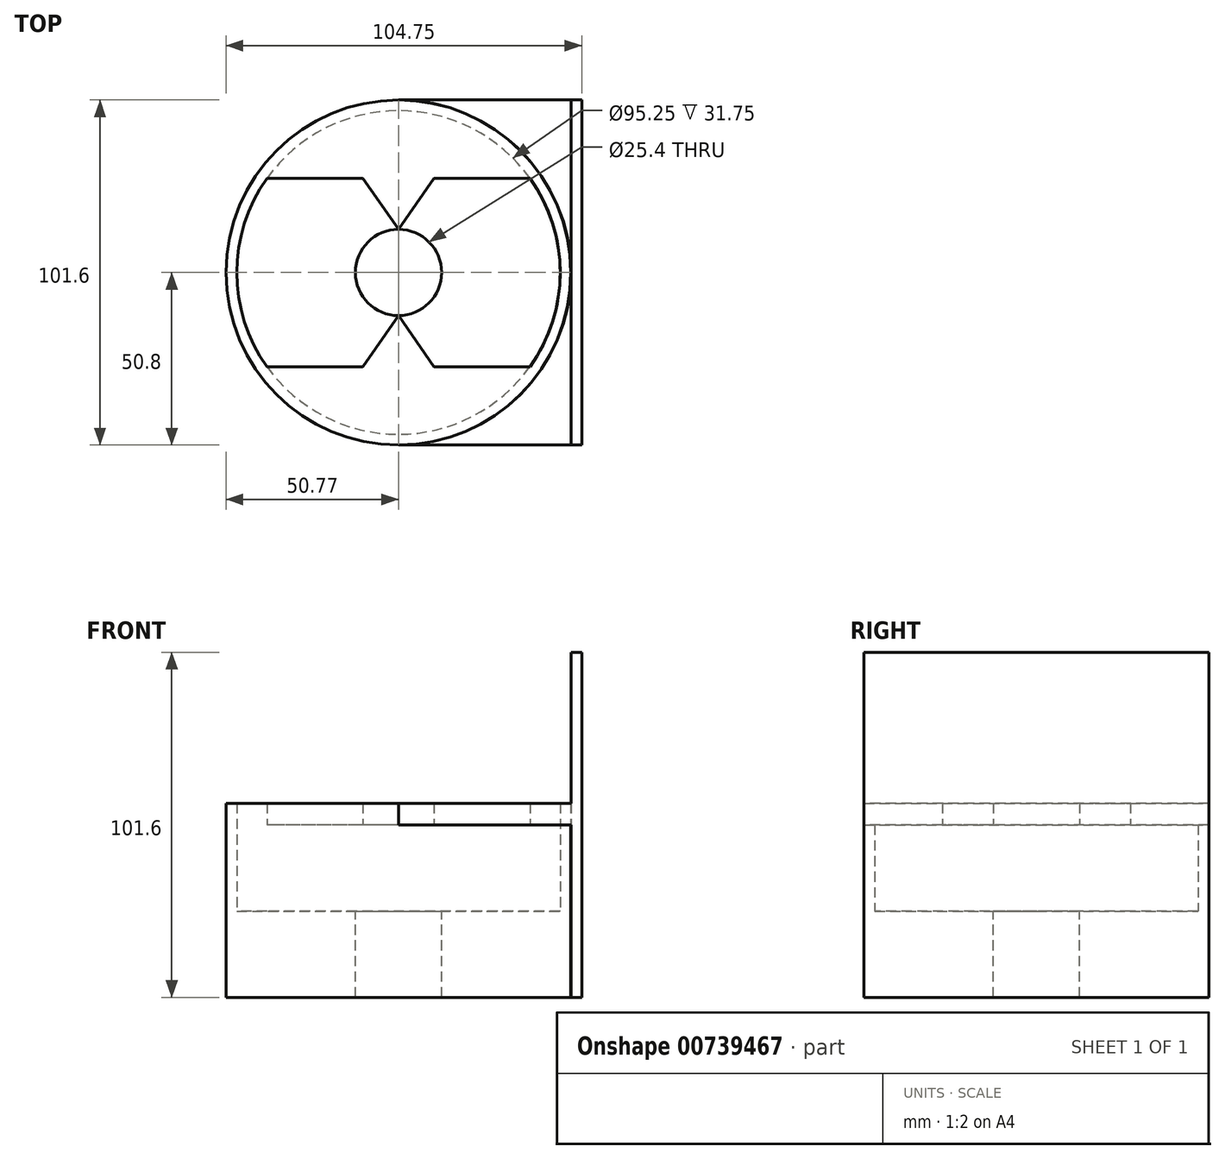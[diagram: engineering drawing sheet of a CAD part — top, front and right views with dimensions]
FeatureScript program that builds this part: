
annotation { "Feature Type Name" : "Feature", "Feature Type Description" : "" }
export const myFeature = defineFeature(function(context is Context, id is Id, definition is map)
    precondition{}
    {
        {
            var Q0;
            Q0=qCreatedBy(makeId("Top.planeOp"),FACE);
            var sketch = newSketch(context, id + "F0", { "sketchPlane" : qUnion([Q0])});
            skCircle(sketch, "E0", {"center": v(0, 0) * mm, "radius": 47.63 * mm});
            skCircle(sketch, "E1", {"center": v(0, 0) * mm, "radius": 50.8 * mm});
            skLineSegment(sketch, "E2.bottom", {"start": v(50.8, 50.8) * mm, "end": v(53.98, 50.8) * mm});
            skLineSegment(sketch, "E2.top", {"start": v(50.8, -50.8) * mm, "end": v(53.98, -50.8) * mm});
            skLineSegment(sketch, "E2.left", {"start": v(50.8, 50.8) * mm, "end": v(50.8, -50.8) * mm});
            skLineSegment(sketch, "E2.right", {"start": v(53.98, 50.8) * mm, "end": v(53.98, -50.8) * mm});
            skLineSegment(sketch, "E3", {"start": v(0, 50.8) * mm, "end": v(96.5, 50.8) * mm});
            skLineSegment(sketch, "E4", {"start": v(0, -50.8) * mm, "end": v(100.01, -50.8) * mm});
            skLineSegment(sketch, "E5", {"start": v(0, 50.8) * mm, "end": v(0, -50.8) * mm});
            skLineSegment(sketch, "E6", {"start": v(21.03, 42.73) * mm, "end": v(0, 12.7) * mm});
            skLineSegment(sketch, "E7", {"start": v(0, 12.7) * mm, "end": v(-21.03, 42.73) * mm});
            skLineSegment(sketch, "E8", {"start": v(21.03, -42.73) * mm, "end": v(0, -12.7) * mm});
            skLineSegment(sketch, "E9", {"start": v(0, -12.7) * mm, "end": v(-21.03, -42.73) * mm});
            skLineSegment(sketch, "E10", {"start": v(10.51, 27.72) * mm, "end": v(38.73, 27.72) * mm});
            skLineSegment(sketch, "E11", {"start": v(10.51, -27.72) * mm, "end": v(38.73, -27.72) * mm});
            skLineSegment(sketch, "E12", {"start": v(-10.51, 27.72) * mm, "end": v(-38.73, 27.72) * mm});
            skLineSegment(sketch, "E13", {"start": v(-10.51, -27.72) * mm, "end": v(-38.73, -27.72) * mm});
            skCircle(sketch, "E14", {"center": v(0, 0) * mm, "radius": 50.77 * mm});
            skSolve(sketch);
        }
        {
            var Q0;
            {var subQ3=sQuery(id+"F0.wireOp",EDGE,"E2.right");Q0=makeQuery(id+"F0.imprint","IMPRINT",FACE,{"disambiguationData":[TD([[makeQuery(id+"F0.imprint","IMPRINT",EDGE,{"derivedFrom":subQ3}),-1.0]])]});}
            extrude(context, id + "F1", {"entities" : qUnion([Q0]), "endBound" : BoundingType.SYMMETRIC, "depth" : 101.6 * mm, "offsetDistance" : 25.4 * mm});
        }
        {
            var Q0;
            {var subQ0=sQuery(id+"F0.wireOp",EDGE,"E3");var subQ3=sQuery(id+"F0.wireOp",EDGE,"E2.left");var subQ5=makeQuery(id+"F0.imprint","INTERSECT",VERTEX,{"derivedFrom":[subQ3,subQ0]});Q0=makeQuery(id+"F0.imprint","IMPRINT",FACE,{"disambiguationData":[TD([[makeQuery(id+"F0.imprint","IMPRINT",EDGE,{"disambiguationData":[TD([[subQ5,-1.0]])],"derivedFrom":subQ3}),-1.0]])]});}
            var Q1;
            {var subQ0=sQuery(id+"F0.wireOp",EDGE,"E4");var subQ3=sQuery(id+"F0.wireOp",EDGE,"E2.left");var subQ5=makeQuery(id+"F0.imprint","INTERSECT",VERTEX,{"derivedFrom":[subQ3,subQ0]});Q1=makeQuery(id+"F0.imprint","IMPRINT",FACE,{"disambiguationData":[TD([[makeQuery(id+"F0.imprint","IMPRINT",EDGE,{"disambiguationData":[TD([[subQ5,1.0]])],"derivedFrom":subQ3}),-1.0]])]});}
            var Q2;
            {var subQ0=sQuery(id+"F0.wireOp",EDGE,"E0");var subQ5=makeQuery(id+"F0.imprint","INTERSECT",VERTEX,{"derivedFrom":[subQ0,sQuery(id+"F0.wireOp",EDGE,"E6")]});Q2=makeQuery(id+"F0.imprint","IMPRINT",FACE,{"disambiguationData":[TD([[makeQuery(id+"F0.imprint","IMPRINT",EDGE,{"disambiguationData":[TD([[subQ5,1.0]])],"derivedFrom":subQ0}),-1.0]])]});}
            var Q3;
            {var subQ0=sQuery(id+"F0.wireOp",EDGE,"E0");var subQ4=makeQuery(id+"F0.imprint","INTERSECT",VERTEX,{"derivedFrom":[subQ0,sQuery(id+"F0.wireOp",EDGE,"E7")]});Q3=makeQuery(id+"F0.imprint","IMPRINT",FACE,{"disambiguationData":[TD([[makeQuery(id+"F0.imprint","IMPRINT",EDGE,{"disambiguationData":[TD([[subQ4,1.0]])],"derivedFrom":subQ0}),-1.0]])]});}
            var Q4;
            {var subQ3=sQuery(id+"F0.wireOp",EDGE,"E12");Q4=makeQuery(id+"F0.imprint","IMPRINT",FACE,{"disambiguationData":[TD([[makeQuery(id+"F0.imprint","IMPRINT",EDGE,{"derivedFrom":subQ3}),-1.0]])]});}
            var Q5;
            {var subQ0=sQuery(id+"F0.wireOp",EDGE,"E7");var subQ1=sQuery(id+"F0.wireOp",EDGE,"E0");var subQ2=makeQuery(id+"F0.imprint","INTERSECT",VERTEX,{"derivedFrom":[subQ1,subQ0]});Q5=makeQuery(id+"F0.imprint","IMPRINT",FACE,{"disambiguationData":[TD([[makeQuery(id+"F0.imprint","IMPRINT",EDGE,{"disambiguationData":[TD([[subQ2,1.0]])],"derivedFrom":subQ1}),1.0]])]});}
            var Q6;
            {var subQ0=sQuery(id+"F0.wireOp",EDGE,"E6");var subQ1=sQuery(id+"F0.wireOp",EDGE,"E0");var subQ2=makeQuery(id+"F0.imprint","INTERSECT",VERTEX,{"derivedFrom":[subQ1,subQ0]});Q6=makeQuery(id+"F0.imprint","IMPRINT",FACE,{"disambiguationData":[TD([[makeQuery(id+"F0.imprint","IMPRINT",EDGE,{"disambiguationData":[TD([[subQ2,-1.0]])],"derivedFrom":subQ1}),1.0]])]});}
            var Q7;
            {var subQ3=sQuery(id+"F0.wireOp",EDGE,"E10");Q7=makeQuery(id+"F0.imprint","IMPRINT",FACE,{"disambiguationData":[TD([[makeQuery(id+"F0.imprint","IMPRINT",EDGE,{"derivedFrom":subQ3}),1.0]])]});}
            var Q8;
            {var subQ3=sQuery(id+"F0.wireOp",EDGE,"E11");Q8=makeQuery(id+"F0.imprint","IMPRINT",FACE,{"disambiguationData":[TD([[makeQuery(id+"F0.imprint","IMPRINT",EDGE,{"derivedFrom":subQ3}),-1.0]])]});}
            var Q9;
            {var subQ0=sQuery(id+"F0.wireOp",EDGE,"E8");var subQ1=sQuery(id+"F0.wireOp",EDGE,"E0");var subQ2=makeQuery(id+"F0.imprint","INTERSECT",VERTEX,{"derivedFrom":[subQ1,subQ0]});Q9=makeQuery(id+"F0.imprint","IMPRINT",FACE,{"disambiguationData":[TD([[makeQuery(id+"F0.imprint","IMPRINT",EDGE,{"disambiguationData":[TD([[subQ2,1.0]])],"derivedFrom":subQ1}),1.0]])]});}
            var Q10;
            {var subQ0=sQuery(id+"F0.wireOp",EDGE,"E9");var subQ1=sQuery(id+"F0.wireOp",EDGE,"E0");var subQ2=makeQuery(id+"F0.imprint","INTERSECT",VERTEX,{"derivedFrom":[subQ1,subQ0]});Q10=makeQuery(id+"F0.imprint","IMPRINT",FACE,{"disambiguationData":[TD([[makeQuery(id+"F0.imprint","IMPRINT",EDGE,{"disambiguationData":[TD([[subQ2,-1.0]])],"derivedFrom":subQ1}),1.0]])]});}
            var Q11;
            {var subQ3=sQuery(id+"F0.wireOp",EDGE,"E13");Q11=makeQuery(id+"F0.imprint","IMPRINT",FACE,{"disambiguationData":[TD([[makeQuery(id+"F0.imprint","IMPRINT",EDGE,{"derivedFrom":subQ3}),1.0]])]});}
            extrude(context, id + "F2", {"entities" : qUnion([Q0, Q1, Q2, Q3, Q4, Q5, Q6, Q7, Q8, Q9, Q10, Q11]), "operationType" : NewBodyOperationType.ADD, "depth" : 6.35 * mm, "offsetDistance" : 25.4 * mm});
        }
        {
            var Q0;
            {var subQ0=sQuery(id+"F0.wireOp",EDGE,"E0");var subQ4=makeQuery(id+"F0.imprint","INTERSECT",VERTEX,{"derivedFrom":[subQ0,sQuery(id+"F0.wireOp",EDGE,"E7")]});Q0=makeQuery(id+"F0.imprint","IMPRINT",FACE,{"disambiguationData":[TD([[makeQuery(id+"F0.imprint","IMPRINT",EDGE,{"disambiguationData":[TD([[subQ4,1.0]])],"derivedFrom":subQ0}),-1.0]])]});}
            var Q1;
            {var subQ0=sQuery(id+"F0.wireOp",EDGE,"E0");var subQ8=makeQuery(id+"F0.imprint","INTERSECT",VERTEX,{"derivedFrom":[subQ0,sQuery(id+"F0.wireOp",EDGE,"E6")]});Q1=makeQuery(id+"F0.imprint","IMPRINT",FACE,{"disambiguationData":[TD([[makeQuery(id+"F0.imprint","IMPRINT",EDGE,{"disambiguationData":[TD([[subQ8,1.0]])],"derivedFrom":subQ0}),-1.0]])]});}
            extrude(context, id + "F3", {"entities" : qUnion([Q0, Q1]), "operationType" : NewBodyOperationType.ADD, "oppositeDirection" : true, "depth" : 25.4 * mm, "offsetDistance" : 25.4 * mm});
        }
        {
            var Q0;
            Q0=makeQuery(id+"F3.opExtrude","CAP_FACE",FACE,{"disambiguationData":[OSD([sQuery(id+"F0.wireOp",EDGE,"E0"),sQuery(id+"F0.wireOp",EDGE,"E14")])],"isStart":false});
            var sketch = newSketch(context, id + "F4", { "sketchPlane" : qUnion([Q0])});
            skCircle(sketch, "E15", {"center": v(0, 0) * mm, "radius": 50.77 * mm});
            skCircle(sketch, "E16", {"center": v(0, 0) * mm, "radius": 12.7 * mm});
            skSolve(sketch);
        }
        {
            var Q0;
            Q0=makeQuery(id+"F4.imprint","IMPRINT",FACE,{"disambiguationData":[TD([[makeQuery(id+"F4.imprint","IMPRINT",EDGE,{"derivedFrom":sQuery(id+"F4.wireOp",EDGE,"E16")}),-1.0]])]});
            var Q1;
            Q1=makeQuery(id+"F4.imprint","IMPRINT",FACE,{"disambiguationData":[TD([[makeQuery(id+"F4.imprint","IMPRINT",EDGE,{"derivedFrom":sQuery(id+"F4.wireOp",EDGE,"E15")}),-1.0]])]});
            extrude(context, id + "F5", {"entities" : qUnion([Q0, Q1]), "operationType" : NewBodyOperationType.ADD, "depth" : 25.4 * mm, "offsetDistance" : 25.4 * mm});
        }
    });
